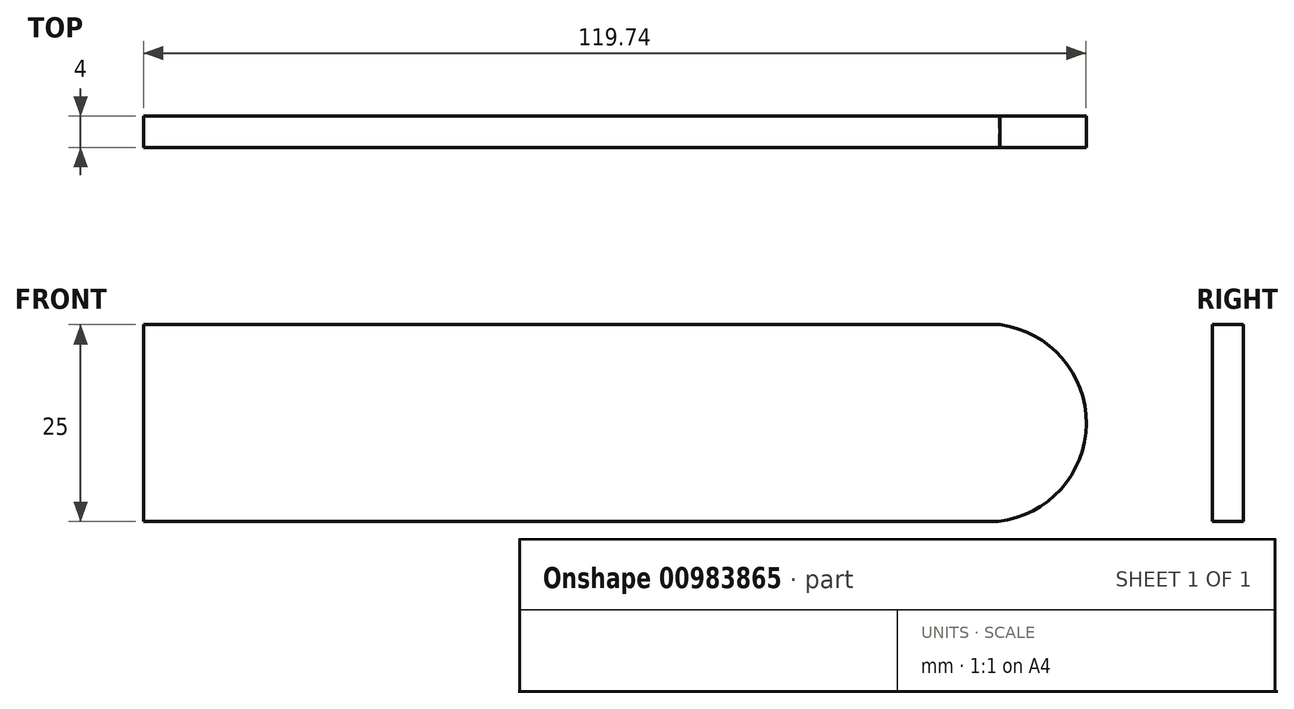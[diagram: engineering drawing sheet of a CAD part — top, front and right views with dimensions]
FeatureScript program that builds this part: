
annotation { "Feature Type Name" : "Feature", "Feature Type Description" : "" }
export const myFeature = defineFeature(function(context is Context, id is Id, definition is map)
    precondition{}
    {
        {
            var Q0;
            Q0=qCreatedBy(makeId("Front.planeOp"),FACE);
            var sketch = newSketch(context, id + "F0", { "sketchPlane" : qUnion([Q0])});
            skLineSegment(sketch, "E0.bottom", {"start": v(-60, -12.5) * mm, "end": v(60, -12.5) * mm});
            skLineSegment(sketch, "E0.top", {"start": v(-60, 12.5) * mm, "end": v(60, 12.5) * mm});
            skLineSegment(sketch, "E0.left", {"start": v(-60, -12.5) * mm, "end": v(-60, 12.5) * mm});
            skLineSegment(sketch, "E0.right", {"start": v(60, -12.5) * mm, "end": v(60, 12.5) * mm});
            skPoint(sketch, "E0.middle", {"position": v(0, 0) * mm});
            skSolve(sketch);
        }
        {
            var Q0;
            Q0=makeQuery(id+"F0.imprint","IMPRINT",FACE,{"disambiguationData":[TD([[makeQuery(id+"F0.imprint","IMPRINT",EDGE,{"derivedFrom":sQuery(id+"F0.wireOp",EDGE,"E0.bottom")}),1.0]])]});
            extrude(context, id + "F1", {"entities" : qUnion([Q0]), "depth" : 4 * mm, "offsetDistance" : 25 * mm});
        }
        {
            var Q0;
            Q0=makeQuery(id+"F1.opExtrude","CAP_FACE",FACE,{"disambiguationData":[OSD([sQuery(id+"F0.wireOp",EDGE,"E0.bottom"),sQuery(id+"F0.wireOp",EDGE,"E0.top"),sQuery(id+"F0.wireOp",EDGE,"E0.left"),sQuery(id+"F0.wireOp",EDGE,"E0.right")])],"isStart":false});
            var sketch = newSketch(context, id + "F2", { "sketchPlane" : qUnion([Q0])});
            skArc(sketch, "E1", {"start": v(48.58, -12.5) * mm, "mid": v(59.74, -0.1) * mm, "end": v(48.82, 12.5) * mm});
            skSolve(sketch);
        }
        {
            var Q0;
            {var subQ0=sQuery(id+"F2.wireOp",EDGE,"E1");Q0=makeQuery(id+"F2.imprint","IMPRINT",FACE,{"disambiguationData":[TD([[makeQuery(id+"F2.imprint","IMPRINT",EDGE,{"derivedFrom":subQ0}),-1.0]])]});}
            extrude(context, id + "F3", {"entities" : qUnion([Q0]), "operationType" : NewBodyOperationType.REMOVE, "oppositeDirection" : true, "depth" : 25 * mm, "offsetDistance" : 25 * mm});
        }
    });
